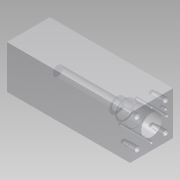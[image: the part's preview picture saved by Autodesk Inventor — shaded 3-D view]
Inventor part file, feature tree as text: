
AUTODESK INVENTOR PART (.ipt)
format: ipt  version: 2014 (Build 180170000, 170)  size: 362,496 bytes
history: native  units: mm
features: other x48, extrude x23, sketch x23
ambient origin geometry x8: Origin, YZ Plane, XZ Plane, XY Plane, X Axis, Y Axis, Z Axis, Center Point
bodies: 实体1 (feature_tree)
feature tree (94):
  extrude  "拉伸1"  Depth=33.7mm
  other  "UCS1"
  other  "UCS2"
  other  "UCS3"
  other  "UCS4"
  other  "UCS5"
  other  "UCS6"
  extrude  "拉伸23"  Depth=35.0mm
  extrude  "拉伸24"  Depth=65.0mm
  extrude  "拉伸25"  Depth=10.0mm
  extrude  "拉伸26"  Depth=43.0mm
  extrude  "拉伸28"  Depth=25.0mm
  extrude  "拉伸29"  Depth=16.0mm
  extrude  "拉伸30"  Depth=152.4mm
  extrude  "拉伸31"  Depth=23.0mm
  extrude  "拉伸32"  Depth=23.0mm
  extrude  "拉伸33"  Depth=23.0mm
  extrude  "拉伸34"  Depth=23.0mm
  extrude  "拉伸35"  Depth=24.0mm TaperAngle=0.0deg
  extrude  "拉伸36"  Depth=24.0mm
  extrude  "拉伸37"  Depth=24.0mm
  extrude  "拉伸39"  Depth=16.0mm TaperAngle=0.0deg
  extrude  "拉伸41"  TaperAngle=0.0deg  [1 undecoded]
  extrude  "拉伸42"  Depth=25.000195mm
  extrude  "拉伸43"  Depth=25.4mm TaperAngle=0.0deg
  extrude  "拉伸54"  Depth=25.4mm
  extrude  "拉伸55"  Depth=4.0mm
  extrude  "拉伸56"  Depth=25.0mm
  extrude  "拉伸57"  TaperAngle=0.0deg  [1 undecoded]
  sketch  "草图1"  dims[d0=70.0mm d1=0.0mm]
  sketch  "草图27"  dims[d2=0.0mm d3=0.0mm d4=0.0mm d5=0.0mm d6=0.0mm d7=0.0mm]
  sketch  "草图28"  dims[d8=0.0mm d9=0.0mm d10=0.0mm d11=0.0mm d12=0.0mm d13=0.0mm]
  sketch  "草图29"  dims[d14=0.0mm d15=0.0mm d16=0.0mm d17=0.0mm d18=0.0mm d19=0.0mm]
  sketch  "草图31"  dims[d20=0.0mm d21=0.0mm d22=0.0mm d23=0.0mm d24=0.0mm d25=0.0mm]
  sketch  "草图32"  dims[d26=0.0mm d27=0.0mm d28=0.0mm d29=0.0mm d30=0.0mm d31=0.0mm]
  sketch  "草图33"  dims[d32=0.0mm d33=0.0mm d34=0.0mm d35=0.0mm d36=0.0mm d37=0.0mm d110=33.7mm]
  sketch  "草图34"  dims[d111=36.0mm d112=35.0mm]
  sketch  "草图35"  dims[d113=65.0mm d114=65.0mm]
  sketch  "草图36"  dims[d115=10.0mm d116=-2.617994mm d117=32.0mm]
  sketch  "草图37"  dims[d118=43.0mm d119=0.0mm d120=26.07mm]
  sketch  "草图38"  dims[d121=13.0mm d122=-2.617994mm d124=25.0mm]
  sketch  "草图39"  dims[d125=56.0mm d126=0.0mm d127=16.0mm]
  sketch  "草图40"  dims[d130=152.4mm d131=0.0mm d132=152.4mm d133=-10.297443mm]
  sketch  "草图41"  dims[d134=6.75mm d135=23.0mm]
  sketch  "草图43"  dims[d136=23.0mm d137=23.0mm]
  sketch  "草图45"  dims[d138=23.0mm d139=23.0mm]
  sketch  "草图46"  dims[d140=23.0mm d141=23.0mm]
  sketch  "草图47"  dims[d142=23.0mm d143=24.0mm d144=0.0mm]
  sketch  "草图64"  dims[d145=24.0mm d146=-10.297443mm d147=24.0mm d148=-10.297443mm]
  sketch  "草图65"  dims[d149=24.0mm d150=-10.297443mm d151=24.0mm d152=-10.297443mm]
  sketch  "草图66"  dims[d153=8.0mm d154=16.0mm d155=0.0mm]
  sketch  "草图67"  dims[d156=4.0mm d160=0.0mm d163=25.000195mm d164=25.4mm d165=0.0mm d166=25.4mm d167=-10.297443mm d170=4.0mm d172=25.0mm d173=0.0mm d176=25.4mm d177=0.0mm d180=25.4mm d181=-10.297443mm d182=4.0mm d183=23.0mm d184=10.5mm d185=8.0mm d186=0.0mm d187=8.0mm d188=-10.297443mm d294=70.0mm d295=200.0mm d296=0.0mm d297=25.0mm d298=4.0mm d299=25.0mm d300=0.0mm d301=25.0mm d302=-10.297443mm d303=0.0mm d304=25.0mm d305=4.0mm d306=27.0mm d307=0.0mm d308=27.0mm d309=-10.297443mm]
  other  "UCS1: YZ 平面"
  other  "UCS1: XZ 平面"
  other  "UCS1: XY 平面"
  other  "UCS1: X 轴"
  other  "UCS1: Y 轴"
  other  "UCS1: Z 轴"
  other  "UCS1: 原点"
  other  "UCS2: YZ 平面"
  other  "UCS2: XZ 平面"
  other  "UCS2: XY 平面"
  other  "UCS2: X 轴"
  other  "UCS2: Y 轴"
  other  "UCS2: Z 轴"
  other  "UCS2: 原点"
  other  "UCS3: YZ 平面"
  other  "UCS3: XZ 平面"
  other  "UCS3: XY 平面"
  other  "UCS3: X 轴"
  other  "UCS3: Y 轴"
  other  "UCS3: Z 轴"
  other  "UCS3: 原点"
  other  "UCS4: YZ 平面"
  other  "UCS4: XZ 平面"
  other  "UCS4: XY 平面"
  other  "UCS4: X 轴"
  other  "UCS4: Y 轴"
  other  "UCS4: Z 轴"
  other  "UCS4: 原点"
  other  "UCS5: YZ 平面"
  other  "UCS5: XZ 平面"
  other  "UCS5: XY 平面"
  other  "UCS5: X 轴"
  other  "UCS5: Y 轴"
  other  "UCS5: Z 轴"
  other  "UCS5: 原点"
  other  "UCS6: YZ 平面"
  other  "UCS6: XZ 平面"
  other  "UCS6: XY 平面"
  other  "UCS6: X 轴"
  other  "UCS6: Y 轴"
  other  "UCS6: Z 轴"
  other  "UCS6: 原点"
note: 2 required parameter values undecoded (feature->parameter linkage not recoverable at this tier; creation-order binding heuristic only, values carry confidence <= 0.55)
